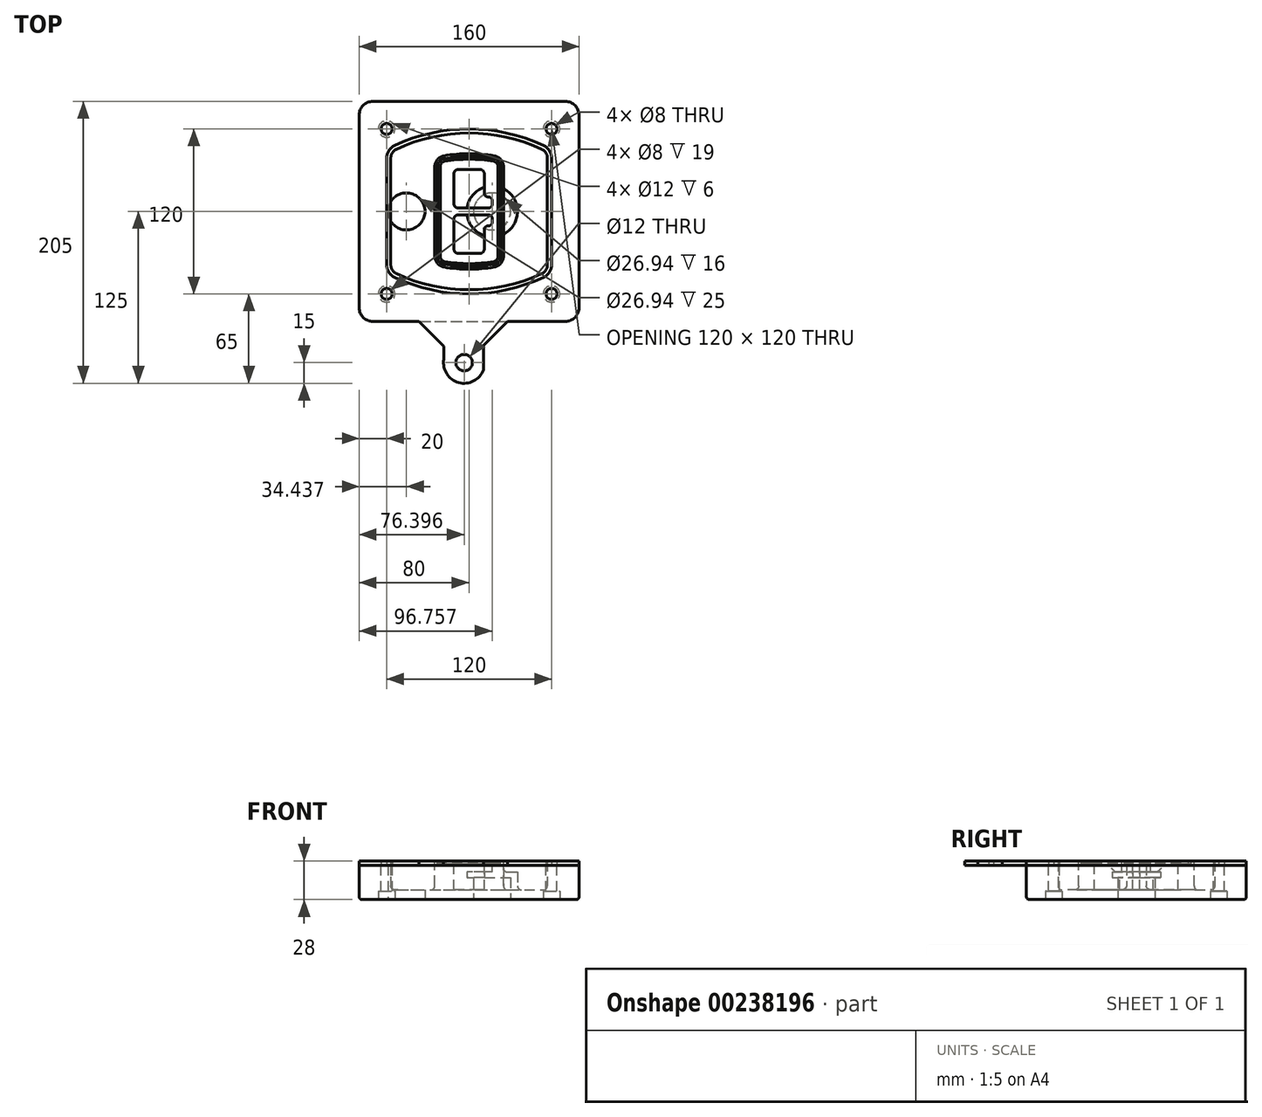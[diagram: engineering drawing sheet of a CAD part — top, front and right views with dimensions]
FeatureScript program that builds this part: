
annotation { "Feature Type Name" : "Feature", "Feature Type Description" : "" }
export const myFeature = defineFeature(function(context is Context, id is Id, definition is map)
    precondition{}
    {
        {
            var Q0;
            Q0=qCreatedBy(makeId("Top.planeOp"),FACE);
            var sketch = newSketch(context, id + "F0", { "sketchPlane" : qUnion([Q0])});
            skPoint(sketch, "E0.rect.middle", {"position": v(0, 0) * mm});
            skLineSegment(sketch, "E1.bottom", {"start": v(-70, -80) * mm, "end": v(70, -80) * mm});
            skLineSegment(sketch, "E1.top", {"start": v(-70, 80) * mm, "end": v(70, 80) * mm});
            skLineSegment(sketch, "E1.left", {"start": v(-80, -70) * mm, "end": v(-80, 70) * mm});
            skLineSegment(sketch, "E1.right", {"start": v(80, -70) * mm, "end": v(80, 70) * mm});
            skLineSegment(sketch, "E2", {"start": v(-80, 80) * mm, "end": v(80, -80) * mm, "construction": true});
            skLineSegment(sketch, "E3", {"start": v(80, 80) * mm, "end": v(-80, -80) * mm, "construction": true});
            skCircle(sketch, "E4", {"center": v(-60, 60) * mm, "radius": 4 * mm});
            skCircle(sketch, "E5", {"center": v(60, 60) * mm, "radius": 4 * mm});
            skCircle(sketch, "E6", {"center": v(60, -60) * mm, "radius": 4 * mm});
            skCircle(sketch, "E7", {"center": v(-60, -60) * mm, "radius": 4 * mm});
            skLineSegment(sketch, "E8", {"start": v(-60, 60) * mm, "end": v(60, 60) * mm, "construction": true});
            skLineSegment(sketch, "E9", {"start": v(60, 60) * mm, "end": v(60, -60) * mm, "construction": true});
            skLineSegment(sketch, "E10", {"start": v(60, -60) * mm, "end": v(-60, -60) * mm, "construction": true});
            skLineSegment(sketch, "E11", {"start": v(-60, -60) * mm, "end": v(-60, 60) * mm, "construction": true});
            skLineSegment(sketch, "E12", {"start": v(-60, 38.83) * mm, "end": v(-60, -38.83) * mm});
            skLineSegment(sketch, "E13", {"start": v(60, 38.83) * mm, "end": v(60, -38.83) * mm});
            skArc(sketch, "E14", {"start": v(54.26, 47.88) * mm, "mid": v(0, 60) * mm, "end": v(-54.26, 47.88) * mm});
            skArc(sketch, "E15", {"start": v(-54.26, -47.88) * mm, "mid": v(0, -60) * mm, "end": v(54.26, -47.88) * mm});
            skLineSegment(sketch, "E16", {"start": v(-60, 0) * mm, "end": v(60, 0) * mm, "construction": true});
            skPoint(sketch, "E17.visualSharp", {"position": v(-60, -45) * mm});
            skArc(sketch, "E17.filletArc", {"start": v(-60, -38.83) * mm, "mid": v(-58.44, -44.2) * mm, "end": v(-54.26, -47.88) * mm});
            skPoint(sketch, "E18.visualSharp", {"position": v(-60, 45) * mm});
            skArc(sketch, "E18.filletArc", {"start": v(-54.26, 47.88) * mm, "mid": v(-58.44, 44.2) * mm, "end": v(-60, 38.83) * mm});
            skPoint(sketch, "E19.visualSharp", {"position": v(60, 45) * mm});
            skArc(sketch, "E19.filletArc", {"start": v(60, 38.83) * mm, "mid": v(58.44, 44.2) * mm, "end": v(54.26, 47.88) * mm});
            skPoint(sketch, "E20.visualSharp", {"position": v(60, -45) * mm});
            skArc(sketch, "E20.filletArc", {"start": v(54.26, -47.88) * mm, "mid": v(58.44, -44.2) * mm, "end": v(60, -38.83) * mm});
            skPoint(sketch, "E21.visualSharp", {"position": v(-80, 80) * mm});
            skArc(sketch, "E21.filletArc", {"start": v(-70, 80) * mm, "mid": v(-77.07, 77.07) * mm, "end": v(-80, 70) * mm});
            skPoint(sketch, "E22.visualSharp", {"position": v(80, 80) * mm});
            skArc(sketch, "E22.filletArc", {"start": v(80, 70) * mm, "mid": v(77.07, 77.07) * mm, "end": v(70, 80) * mm});
            skPoint(sketch, "E23.visualSharp", {"position": v(80, -80) * mm});
            skArc(sketch, "E23.filletArc", {"start": v(70, -80) * mm, "mid": v(77.07, -77.07) * mm, "end": v(80, -70) * mm});
            skPoint(sketch, "E24.visualSharp", {"position": v(-80, -80) * mm});
            skArc(sketch, "E24.filletArc", {"start": v(-80, -70) * mm, "mid": v(-77.07, -77.07) * mm, "end": v(-70, -80) * mm});
            skArc(sketch, "E25.0", {"start": v(57, 38.83) * mm, "mid": v(55.9, 42.58) * mm, "end": v(52.98, 45.17) * mm});
            skLineSegment(sketch, "E25.1", {"start": v(57, 38.83) * mm, "end": v(57, -38.83) * mm});
            skArc(sketch, "E25.2", {"start": v(52.98, -45.17) * mm, "mid": v(55.9, -42.58) * mm, "end": v(57, -38.83) * mm});
            skArc(sketch, "E25.3", {"start": v(-52.98, -45.17) * mm, "mid": v(0, -57) * mm, "end": v(52.98, -45.17) * mm});
            skArc(sketch, "E25.4", {"start": v(-57, -38.83) * mm, "mid": v(-55.9, -42.58) * mm, "end": v(-52.98, -45.17) * mm});
            skArc(sketch, "E25.5", {"start": v(52.98, 45.17) * mm, "mid": v(0, 57) * mm, "end": v(-52.98, 45.17) * mm});
            skLineSegment(sketch, "E25.6", {"start": v(-57, 38.83) * mm, "end": v(-57, -38.83) * mm});
            skArc(sketch, "E25.7", {"start": v(-52.98, 45.17) * mm, "mid": v(-55.9, 42.58) * mm, "end": v(-57, 38.83) * mm});
            skArc(sketch, "E26.0", {"start": v(-55.96, 51.5) * mm, "mid": v(-61.82, 46.33) * mm, "end": v(-64, 38.83) * mm});
            skArc(sketch, "E26.1", {"start": v(55.96, 51.5) * mm, "mid": v(0, 64) * mm, "end": v(-55.96, 51.5) * mm});
            skArc(sketch, "E26.2", {"start": v(64, 38.83) * mm, "mid": v(61.82, 46.33) * mm, "end": v(55.96, 51.5) * mm});
            skLineSegment(sketch, "E26.3", {"start": v(64, 38.83) * mm, "end": v(64, -38.83) * mm});
            skArc(sketch, "E26.4", {"start": v(55.96, -51.5) * mm, "mid": v(61.82, -46.33) * mm, "end": v(64, -38.83) * mm});
            skLineSegment(sketch, "E26.5", {"start": v(-64, 38.83) * mm, "end": v(-64, -38.83) * mm});
            skArc(sketch, "E26.6", {"start": v(-55.96, -51.5) * mm, "mid": v(0, -64) * mm, "end": v(55.96, -51.5) * mm});
            skArc(sketch, "E26.7", {"start": v(-64, -38.83) * mm, "mid": v(-61.82, -46.33) * mm, "end": v(-55.96, -51.5) * mm});
            skSolve(sketch);
        }
        {
            var Q0;
            Q0=makeQuery(id+"F0.imprint","IMPRINT",FACE,{"disambiguationData":[TD([[makeQuery(id+"F0.imprint","IMPRINT",EDGE,{"derivedFrom":sQuery(id+"F0.wireOp",EDGE,"E1.bottom")}),1.0]])]});
            var Q1;
            Q1=makeQuery(id+"F0.imprint","IMPRINT",FACE,{"disambiguationData":[TD([[makeQuery(id+"F0.imprint","IMPRINT",EDGE,{"derivedFrom":sQuery(id+"F0.wireOp",EDGE,"E12")}),1.0]])]});
            var Q2;
            Q2=makeQuery(id+"F0.imprint","IMPRINT",FACE,{"disambiguationData":[TD([[makeQuery(id+"F0.imprint","IMPRINT",EDGE,{"derivedFrom":sQuery(id+"F0.wireOp",EDGE,"E25.0")}),1.0]])]});
            var Q3;
            Q3=makeQuery(id+"F0.imprint","IMPRINT",FACE,{"disambiguationData":[TD([[makeQuery(id+"F0.imprint","IMPRINT",EDGE,{"derivedFrom":sQuery(id+"F0.wireOp",EDGE,"E12")}),-1.0]])]});
            extrude(context, id + "F1", {"entities" : qUnion([Q0, Q1, Q2, Q3]), "oppositeDirection" : true, "depth" : 25 * mm});
        }
        {
            var Q0;
            Q0=makeQuery(id+"F0.imprint","IMPRINT",FACE,{"disambiguationData":[TD([[makeQuery(id+"F0.imprint","IMPRINT",EDGE,{"derivedFrom":sQuery(id+"F0.wireOp",EDGE,"E12")}),1.0]])]});
            extrude(context, id + "F2", {"entities" : qUnion([Q0]), "operationType" : NewBodyOperationType.ADD, "depth" : 3 * mm});
        }
        {
            var Q0;
            Q0=makeQuery(id+"F0.imprint","IMPRINT",FACE,{"disambiguationData":[TD([[makeQuery(id+"F0.imprint","IMPRINT",EDGE,{"derivedFrom":sQuery(id+"F0.wireOp",EDGE,"E25.0")}),1.0]])]});
            extrude(context, id + "F3", {"entities" : qUnion([Q0]), "operationType" : NewBodyOperationType.REMOVE, "oppositeDirection" : true, "depth" : 18 * mm});
        }
        {
            var Q0;
            Q0=makeQuery(id+"F2.opExtrude","CAP_FACE",FACE,{"disambiguationData":[OSD([sQuery(id+"F0.wireOp",EDGE,"E12"),sQuery(id+"F0.wireOp",EDGE,"E13"),sQuery(id+"F0.wireOp",EDGE,"E14"),sQuery(id+"F0.wireOp",EDGE,"E15"),sQuery(id+"F0.wireOp",EDGE,"E17.filletArc"),sQuery(id+"F0.wireOp",EDGE,"E18.filletArc"),sQuery(id+"F0.wireOp",EDGE,"E19.filletArc"),sQuery(id+"F0.wireOp",EDGE,"E20.filletArc"),sQuery(id+"F0.wireOp",EDGE,"E25.0"),sQuery(id+"F0.wireOp",EDGE,"E25.1"),sQuery(id+"F0.wireOp",EDGE,"E25.2"),sQuery(id+"F0.wireOp",EDGE,"E25.3"),sQuery(id+"F0.wireOp",EDGE,"E25.4"),sQuery(id+"F0.wireOp",EDGE,"E25.5"),sQuery(id+"F0.wireOp",EDGE,"E25.6"),sQuery(id+"F0.wireOp",EDGE,"E25.7")])],"isStart":false});
            var sketch = newSketch(context, id + "F4", { "sketchPlane" : qUnion([Q0])});
            skArc(sketch, "E27.0", {"start": v(-18.34, -40.45) * mm, "mid": v(0, -42) * mm, "end": v(18.34, -40.45) * mm});
            skArc(sketch, "E28.0", {"start": v(18.34, 40.45) * mm, "mid": v(0, 42) * mm, "end": v(-18.34, 40.45) * mm});
            skLineSegment(sketch, "E29", {"start": v(-25, 32.57) * mm, "end": v(-25, -32.57) * mm});
            skLineSegment(sketch, "E30", {"start": v(25, 32.57) * mm, "end": v(25, -32.57) * mm});
            skLineSegment(sketch, "E31", {"start": v(-25, 39.1) * mm, "end": v(25, 39.1) * mm, "construction": true});
            skLineSegment(sketch, "E32", {"start": v(-25, -39.1) * mm, "end": v(25, -39.1) * mm, "construction": true});
            skPoint(sketch, "E33.visualSharp", {"position": v(-25, 39.1) * mm});
            skArc(sketch, "E33.filletArc", {"start": v(-18.34, 40.45) * mm, "mid": v(-23.11, 37.73) * mm, "end": v(-25, 32.57) * mm});
            skPoint(sketch, "E34.visualSharp", {"position": v(25, 39.1) * mm});
            skArc(sketch, "E34.filletArc", {"start": v(25, 32.57) * mm, "mid": v(23.11, 37.73) * mm, "end": v(18.34, 40.45) * mm});
            skPoint(sketch, "E35.visualSharp", {"position": v(25, -39.1) * mm});
            skArc(sketch, "E35.filletArc", {"start": v(18.34, -40.45) * mm, "mid": v(23.11, -37.73) * mm, "end": v(25, -32.57) * mm});
            skPoint(sketch, "E36.visualSharp", {"position": v(-25, -39.1) * mm});
            skArc(sketch, "E36.filletArc", {"start": v(-25, -32.57) * mm, "mid": v(-23.11, -37.73) * mm, "end": v(-18.34, -40.45) * mm});
            skArc(sketch, "E37.0", {"start": v(52.98, 45.17) * mm, "mid": v(0, 57) * mm, "end": v(-52.98, 45.17) * mm});
            skArc(sketch, "E37.1", {"start": v(-52.98, 45.17) * mm, "mid": v(-55.9, 42.58) * mm, "end": v(-57, 38.83) * mm});
            skLineSegment(sketch, "E37.2", {"start": v(-57, 38.83) * mm, "end": v(-57, -38.83) * mm});
            skArc(sketch, "E37.3", {"start": v(-57, -38.83) * mm, "mid": v(-55.9, -42.58) * mm, "end": v(-52.98, -45.17) * mm});
            skArc(sketch, "E37.4", {"start": v(-52.98, -45.17) * mm, "mid": v(0, -57) * mm, "end": v(52.98, -45.17) * mm});
            skArc(sketch, "E37.5", {"start": v(52.98, -45.17) * mm, "mid": v(55.9, -42.58) * mm, "end": v(57, -38.83) * mm});
            skLineSegment(sketch, "E37.6", {"start": v(57, 38.83) * mm, "end": v(57, -38.83) * mm});
            skArc(sketch, "E37.7", {"start": v(57, 38.83) * mm, "mid": v(55.9, 42.58) * mm, "end": v(52.98, 45.17) * mm});
            skLineSegment(sketch, "E38.0", {"start": v(23, 32.57) * mm, "end": v(23, -32.57) * mm});
            skArc(sketch, "E38.1", {"start": v(18, -38.48) * mm, "mid": v(21.58, -36.44) * mm, "end": v(23, -32.57) * mm});
            skArc(sketch, "E38.2", {"start": v(-18, -38.48) * mm, "mid": v(0, -40) * mm, "end": v(18, -38.48) * mm});
            skArc(sketch, "E38.3", {"start": v(-23, -32.57) * mm, "mid": v(-21.58, -36.44) * mm, "end": v(-18, -38.48) * mm});
            skLineSegment(sketch, "E38.4", {"start": v(-23, 32.57) * mm, "end": v(-23, -32.57) * mm});
            skArc(sketch, "E38.5", {"start": v(23, 32.57) * mm, "mid": v(21.58, 36.44) * mm, "end": v(18, 38.48) * mm});
            skArc(sketch, "E38.6", {"start": v(-18, 38.48) * mm, "mid": v(-21.58, 36.44) * mm, "end": v(-23, 32.57) * mm});
            skArc(sketch, "E38.7", {"start": v(18, 38.48) * mm, "mid": v(0, 40) * mm, "end": v(-18, 38.48) * mm});
            skArc(sketch, "E39.0", {"start": v(21, 32.57) * mm, "mid": v(20.06, 35.15) * mm, "end": v(17.67, 36.5) * mm});
            skLineSegment(sketch, "E39.1", {"start": v(21, 32.57) * mm, "end": v(21, -32.57) * mm});
            skArc(sketch, "E39.2", {"start": v(17.67, -36.5) * mm, "mid": v(20.06, -35.15) * mm, "end": v(21, -32.57) * mm});
            skArc(sketch, "E39.3", {"start": v(-17.67, -36.5) * mm, "mid": v(0, -38) * mm, "end": v(17.67, -36.5) * mm});
            skArc(sketch, "E39.4", {"start": v(-21, -32.57) * mm, "mid": v(-20.06, -35.15) * mm, "end": v(-17.67, -36.5) * mm});
            skArc(sketch, "E39.5", {"start": v(17.67, 36.5) * mm, "mid": v(0, 38) * mm, "end": v(-17.67, 36.5) * mm});
            skLineSegment(sketch, "E39.6", {"start": v(-21, 32.57) * mm, "end": v(-21, -32.57) * mm});
            skArc(sketch, "E39.7", {"start": v(-17.67, 36.5) * mm, "mid": v(-20.06, 35.15) * mm, "end": v(-21, 32.57) * mm});
            skLineSegment(sketch, "E40", {"start": v(-25, 0) * mm, "end": v(25, 0) * mm, "construction": true});
            skLineSegment(sketch, "E41", {"start": v(-11, 5.5) * mm, "end": v(-11, 27.5) * mm});
            skLineSegment(sketch, "E42", {"start": v(-8, 30.5) * mm, "end": v(8, 30.5) * mm});
            skLineSegment(sketch, "E43", {"start": v(11, 27.5) * mm, "end": v(11, 13.5) * mm});
            skLineSegment(sketch, "E44", {"start": v(14, 10.5) * mm, "end": v(14, 10.5) * mm});
            skLineSegment(sketch, "E45", {"start": v(17, 7.5) * mm, "end": v(17, 5.5) * mm});
            skLineSegment(sketch, "E46", {"start": v(14, 2.5) * mm, "end": v(-8, 2.5) * mm});
            skPoint(sketch, "E47.visualSharp", {"position": v(-11, 30.5) * mm});
            skArc(sketch, "E47.filletArc", {"start": v(-8, 30.5) * mm, "mid": v(-10.12, 29.62) * mm, "end": v(-11, 27.5) * mm});
            skPoint(sketch, "E48.visualSharp", {"position": v(11, 30.5) * mm});
            skArc(sketch, "E48.filletArc", {"start": v(11, 27.5) * mm, "mid": v(10.12, 29.62) * mm, "end": v(8, 30.5) * mm});
            skPoint(sketch, "E49.visualSharp", {"position": v(11, 10.5) * mm});
            skArc(sketch, "E49.filletArc", {"start": v(11, 13.5) * mm, "mid": v(11.88, 11.38) * mm, "end": v(14, 10.5) * mm});
            skPoint(sketch, "E50.visualSharp", {"position": v(17, 10.5) * mm});
            skArc(sketch, "E50.filletArc", {"start": v(17, 7.5) * mm, "mid": v(16.12, 9.62) * mm, "end": v(14, 10.5) * mm});
            skPoint(sketch, "E51.visualSharp", {"position": v(17, 2.5) * mm});
            skArc(sketch, "E51.filletArc", {"start": v(14, 2.5) * mm, "mid": v(16.12, 3.38) * mm, "end": v(17, 5.5) * mm});
            skPoint(sketch, "E52.visualSharp", {"position": v(-11, 2.5) * mm});
            skArc(sketch, "E52.filletArc", {"start": v(-11, 5.5) * mm, "mid": v(-10.12, 3.38) * mm, "end": v(-8, 2.5) * mm});
            skLineSegment(sketch, "E53.0.MirrorCS", {"start": v(14, -2.5) * mm, "end": v(-8, -2.5) * mm});
            skArc(sketch, "E54.0.MirrorCS", {"start": v(-11, -5.5) * mm, "mid": v(-10.12, -3.38) * mm, "end": v(-8, -2.5) * mm});
            skLineSegment(sketch, "E55.0.MirrorCS", {"start": v(-11, -5.5) * mm, "end": v(-11, -27.5) * mm});
            skArc(sketch, "E56.0.MirrorCS", {"start": v(-8, -30.5) * mm, "mid": v(-10.12, -29.62) * mm, "end": v(-11, -27.5) * mm});
            skLineSegment(sketch, "E57.0.MirrorCS", {"start": v(-8, -30.5) * mm, "end": v(8, -30.5) * mm});
            skArc(sketch, "E58.0.MirrorCS", {"start": v(11, -27.5) * mm, "mid": v(10.12, -29.62) * mm, "end": v(8, -30.5) * mm});
            skLineSegment(sketch, "E59.0.MirrorCS", {"start": v(11, -27.5) * mm, "end": v(11, -13.5) * mm});
            skArc(sketch, "E60.0.MirrorCS", {"start": v(11, -13.5) * mm, "mid": v(11.88, -11.38) * mm, "end": v(14, -10.5) * mm});
            skArc(sketch, "E61.0.MirrorCS", {"start": v(17, -7.5) * mm, "mid": v(16.12, -9.62) * mm, "end": v(14, -10.5) * mm});
            skLineSegment(sketch, "E62.0.MirrorCS", {"start": v(17, -7.5) * mm, "end": v(17, -5.5) * mm});
            skArc(sketch, "E63.0.MirrorCS", {"start": v(14, -2.5) * mm, "mid": v(16.12, -3.38) * mm, "end": v(17, -5.5) * mm});
            skSolve(sketch);
        }
        {
            var Q0;
            Q0=makeQuery(id+"F4.imprint","IMPRINT",FACE,{"disambiguationData":[TD([[makeQuery(id+"F4.imprint","IMPRINT",EDGE,{"derivedFrom":sQuery(id+"F4.wireOp",EDGE,"E27.0")}),1.0]])]});
            var Q1;
            Q1=makeQuery(id+"F4.imprint","IMPRINT",FACE,{"disambiguationData":[TD([[makeQuery(id+"F4.imprint","IMPRINT",EDGE,{"derivedFrom":sQuery(id+"F4.wireOp",EDGE,"E38.0")}),-1.0]])]});
            var Q2;
            Q2=makeQuery(id+"F4.imprint","IMPRINT",FACE,{"disambiguationData":[TD([[makeQuery(id+"F4.imprint","IMPRINT",EDGE,{"derivedFrom":sQuery(id+"F4.wireOp",EDGE,"E39.0")}),1.0]])]});
            extrude(context, id + "F5", {"entities" : qUnion([Q0, Q1, Q2]), "operationType" : NewBodyOperationType.ADD, "endBound" : BoundingType.UP_TO_NEXT, "oppositeDirection" : true, "depth" : 25 * mm});
        }
        {
            var Q0;
            Q0=makeQuery(id+"F4.imprint","IMPRINT",FACE,{"disambiguationData":[TD([[makeQuery(id+"F4.imprint","IMPRINT",EDGE,{"derivedFrom":sQuery(id+"F4.wireOp",EDGE,"E38.0")}),-1.0]])]});
            extrude(context, id + "F6", {"entities" : qUnion([Q0]), "operationType" : NewBodyOperationType.REMOVE, "oppositeDirection" : true, "depth" : 2 * mm});
        }
        {
            var Q0;
            Q0=makeQuery(id+"F1.opExtrude","CAP_FACE",FACE,{"disambiguationData":[OSD([sQuery(id+"F0.wireOp",EDGE,"E1.bottom"),sQuery(id+"F0.wireOp",EDGE,"E1.top"),sQuery(id+"F0.wireOp",EDGE,"E1.left"),sQuery(id+"F0.wireOp",EDGE,"E1.right"),sQuery(id+"F0.wireOp",EDGE,"E4"),sQuery(id+"F0.wireOp",EDGE,"E5"),sQuery(id+"F0.wireOp",EDGE,"E6"),sQuery(id+"F0.wireOp",EDGE,"E7"),sQuery(id+"F0.wireOp",EDGE,"E21.filletArc"),sQuery(id+"F0.wireOp",EDGE,"E22.filletArc"),sQuery(id+"F0.wireOp",EDGE,"E23.filletArc"),sQuery(id+"F0.wireOp",EDGE,"E24.filletArc")])],"isStart":false});
            var sketch = newSketch(context, id + "F7", { "sketchPlane" : qUnion([Q0])});
            skCircle(sketch, "E64", {"center": v(16.76, 0) * mm, "radius": 13.47 * mm});
            skCircle(sketch, "E65", {"center": v(-45.56, 0) * mm, "radius": 13.47 * mm});
            skLineSegment(sketch, "E66", {"start": v(80, 0) * mm, "end": v(-80, 0) * mm});
            skCircle(sketch, "E67", {"center": v(16.76, 0) * mm, "radius": 18.47 * mm});
            skCircle(sketch, "E68", {"center": v(60, -60) * mm, "radius": 6 * mm});
            skCircle(sketch, "E69", {"center": v(-60, -60) * mm, "radius": 6 * mm});
            skCircle(sketch, "E70", {"center": v(-60, 60) * mm, "radius": 6 * mm});
            skCircle(sketch, "E71", {"center": v(60, 60) * mm, "radius": 6 * mm});
            skSolve(sketch);
        }
        {
            var Q0;
            {var subQ1=sQuery(id+"F7.wireOp",EDGE,"E66");var subQ4=sQuery(id+"F7.wireOp",EDGE,"E64");var subQ6=makeQuery(id+"F7.imprint","INTERSECT",VERTEX,{"disambiguationData":[OD(0.0)],"derivedFrom":[subQ4,subQ1]});Q0=makeQuery(id+"F7.imprint","IMPRINT",FACE,{"disambiguationData":[TD([[makeQuery(id+"F7.imprint","IMPRINT",EDGE,{"disambiguationData":[TD([[subQ6,-1.0]])],"derivedFrom":subQ4}),-1.0]])]});}
            var Q1;
            {var subQ0=sQuery(id+"F7.wireOp",EDGE,"E66");var subQ1=sQuery(id+"F7.wireOp",EDGE,"E64");var subQ3=makeQuery(id+"F7.imprint","INTERSECT",VERTEX,{"disambiguationData":[OD(0.0)],"derivedFrom":[subQ1,subQ0]});Q1=makeQuery(id+"F7.imprint","IMPRINT",FACE,{"disambiguationData":[TD([[makeQuery(id+"F7.imprint","IMPRINT",EDGE,{"disambiguationData":[TD([[subQ3,-1.0]])],"derivedFrom":subQ1}),1.0]])]});}
            var Q2;
            {var subQ0=sQuery(id+"F7.wireOp",EDGE,"E66");var subQ1=sQuery(id+"F7.wireOp",EDGE,"E64");var subQ3=makeQuery(id+"F7.imprint","INTERSECT",VERTEX,{"disambiguationData":[OD(0.0)],"derivedFrom":[subQ1,subQ0]});Q2=makeQuery(id+"F7.imprint","IMPRINT",FACE,{"disambiguationData":[TD([[makeQuery(id+"F7.imprint","IMPRINT",EDGE,{"disambiguationData":[TD([[subQ3,1.0]])],"derivedFrom":subQ1}),1.0]])]});}
            var Q3;
            {var subQ1=sQuery(id+"F7.wireOp",EDGE,"E66");var subQ4=sQuery(id+"F7.wireOp",EDGE,"E64");var subQ6=makeQuery(id+"F7.imprint","INTERSECT",VERTEX,{"disambiguationData":[OD(0.0)],"derivedFrom":[subQ4,subQ1]});Q3=makeQuery(id+"F7.imprint","IMPRINT",FACE,{"disambiguationData":[TD([[makeQuery(id+"F7.imprint","IMPRINT",EDGE,{"disambiguationData":[TD([[subQ6,1.0]])],"derivedFrom":subQ4}),-1.0]])]});}
            extrude(context, id + "F8", {"entities" : qUnion([Q0, Q1, Q2, Q3]), "operationType" : NewBodyOperationType.ADD, "oppositeDirection" : true, "depth" : 20 * mm});
        }
        {
            var Q0;
            {var subQ0=sQuery(id+"F7.wireOp",EDGE,"E66");var subQ1=sQuery(id+"F7.wireOp",EDGE,"E64");var subQ3=makeQuery(id+"F7.imprint","INTERSECT",VERTEX,{"disambiguationData":[OD(0.0)],"derivedFrom":[subQ1,subQ0]});Q0=makeQuery(id+"F7.imprint","IMPRINT",FACE,{"disambiguationData":[TD([[makeQuery(id+"F7.imprint","IMPRINT",EDGE,{"disambiguationData":[TD([[subQ3,-1.0]])],"derivedFrom":subQ1}),1.0]])]});}
            var Q1;
            {var subQ0=sQuery(id+"F7.wireOp",EDGE,"E66");var subQ1=sQuery(id+"F7.wireOp",EDGE,"E64");var subQ3=makeQuery(id+"F7.imprint","INTERSECT",VERTEX,{"disambiguationData":[OD(0.0)],"derivedFrom":[subQ1,subQ0]});Q1=makeQuery(id+"F7.imprint","IMPRINT",FACE,{"disambiguationData":[TD([[makeQuery(id+"F7.imprint","IMPRINT",EDGE,{"disambiguationData":[TD([[subQ3,1.0]])],"derivedFrom":subQ1}),1.0]])]});}
            extrude(context, id + "F9", {"entities" : qUnion([Q0, Q1]), "operationType" : NewBodyOperationType.REMOVE, "oppositeDirection" : true, "depth" : 16 * mm});
        }
        {
            var Q0;
            {var subQ0=sQuery(id+"F7.wireOp",EDGE,"E66");var subQ1=sQuery(id+"F7.wireOp",EDGE,"E65");var subQ3=makeQuery(id+"F7.imprint","INTERSECT",VERTEX,{"disambiguationData":[OD(0.0)],"derivedFrom":[subQ1,subQ0]});Q0=makeQuery(id+"F7.imprint","IMPRINT",FACE,{"disambiguationData":[TD([[makeQuery(id+"F7.imprint","IMPRINT",EDGE,{"disambiguationData":[TD([[subQ3,-1.0]])],"derivedFrom":subQ1}),1.0]])]});}
            var Q1;
            {var subQ0=sQuery(id+"F7.wireOp",EDGE,"E66");var subQ1=sQuery(id+"F7.wireOp",EDGE,"E65");var subQ3=makeQuery(id+"F7.imprint","INTERSECT",VERTEX,{"disambiguationData":[OD(0.0)],"derivedFrom":[subQ1,subQ0]});Q1=makeQuery(id+"F7.imprint","IMPRINT",FACE,{"disambiguationData":[TD([[makeQuery(id+"F7.imprint","IMPRINT",EDGE,{"disambiguationData":[TD([[subQ3,1.0]])],"derivedFrom":subQ1}),1.0]])]});}
            extrude(context, id + "F10", {"entities" : qUnion([Q0, Q1]), "operationType" : NewBodyOperationType.REMOVE, "oppositeDirection" : true, "depth" : 25 * mm});
        }
        {
            var Q0;
            Q0=makeQuery(id+"F7.imprint","IMPRINT",FACE,{"disambiguationData":[TD([[makeQuery(id+"F7.imprint","IMPRINT",EDGE,{"derivedFrom":sQuery(id+"F7.wireOp",EDGE,"E68")}),1.0]])]});
            var Q1;
            Q1=makeQuery(id+"F7.imprint","IMPRINT",FACE,{"disambiguationData":[TD([[makeQuery(id+"F7.imprint","IMPRINT",EDGE,{"derivedFrom":makeQuery(id+"F1.opExtrude","CAP_EDGE",EDGE,{"disambiguationData":[OSD([sQuery(id+"F0.wireOp",EDGE,"E5")])],"isStart":false})}),-1.0]])]});
            var Q2;
            Q2=makeQuery(id+"F7.imprint","IMPRINT",FACE,{"disambiguationData":[TD([[makeQuery(id+"F7.imprint","IMPRINT",EDGE,{"derivedFrom":sQuery(id+"F7.wireOp",EDGE,"E69")}),1.0]])]});
            var Q3;
            Q3=makeQuery(id+"F7.imprint","IMPRINT",FACE,{"disambiguationData":[TD([[makeQuery(id+"F7.imprint","IMPRINT",EDGE,{"derivedFrom":makeQuery(id+"F1.opExtrude","CAP_EDGE",EDGE,{"disambiguationData":[OSD([sQuery(id+"F0.wireOp",EDGE,"E4")])],"isStart":false})}),-1.0]])]});
            var Q4;
            Q4=makeQuery(id+"F7.imprint","IMPRINT",FACE,{"disambiguationData":[TD([[makeQuery(id+"F7.imprint","IMPRINT",EDGE,{"derivedFrom":sQuery(id+"F7.wireOp",EDGE,"E70")}),1.0]])]});
            var Q5;
            Q5=makeQuery(id+"F7.imprint","IMPRINT",FACE,{"disambiguationData":[TD([[makeQuery(id+"F7.imprint","IMPRINT",EDGE,{"derivedFrom":makeQuery(id+"F1.opExtrude","CAP_EDGE",EDGE,{"disambiguationData":[OSD([sQuery(id+"F0.wireOp",EDGE,"E7")])],"isStart":false})}),-1.0]])]});
            var Q6;
            Q6=makeQuery(id+"F7.imprint","IMPRINT",FACE,{"disambiguationData":[TD([[makeQuery(id+"F7.imprint","IMPRINT",EDGE,{"derivedFrom":sQuery(id+"F7.wireOp",EDGE,"E71")}),1.0]])]});
            var Q7;
            Q7=makeQuery(id+"F7.imprint","IMPRINT",FACE,{"disambiguationData":[TD([[makeQuery(id+"F7.imprint","IMPRINT",EDGE,{"derivedFrom":makeQuery(id+"F1.opExtrude","CAP_EDGE",EDGE,{"disambiguationData":[OSD([sQuery(id+"F0.wireOp",EDGE,"E6")])],"isStart":false})}),-1.0]])]});
            extrude(context, id + "F11", {"entities" : qUnion([Q0, Q1, Q2, Q3, Q4, Q5, Q6, Q7]), "operationType" : NewBodyOperationType.REMOVE, "oppositeDirection" : true, "depth" : 6 * mm});
        }
        {
            var Q0;
            Q0=makeQuery(id+"F9.boolean.opBoolean","COPY",FACE,{"derivedFrom":makeQuery(id+"F9.opExtrude","CAP_FACE",FACE,{"disambiguationData":[OSD([sQuery(id+"F7.wireOp",EDGE,"E64")])],"isStart":false})});
            var sketch = newSketch(context, id + "F12", { "sketchPlane" : qUnion([Q0])});
            skArc(sketch, "E72.0", {"start": v(11, 17.55) * mm, "mid": v(2.57, 11.82) * mm, "end": v(-1.54, 2.5) * mm});
            skArc(sketch, "E72.1", {"start": v(-1.54, -2.5) * mm, "mid": v(2.57, -11.82) * mm, "end": v(11, -17.55) * mm});
            skLineSegment(sketch, "E73", {"start": v(-1.54, -2.5) * mm, "end": v(14, -2.5) * mm});
            skLineSegment(sketch, "E74.0", {"start": v(14, 2.5) * mm, "end": v(-1.54, 2.5) * mm});
            skArc(sketch, "E74.1", {"start": v(14, 2.5) * mm, "mid": v(16.12, 3.38) * mm, "end": v(17, 5.5) * mm});
            skLineSegment(sketch, "E74.2", {"start": v(17, 7.5) * mm, "end": v(17, 5.5) * mm});
            skArc(sketch, "E74.3", {"start": v(17, 7.5) * mm, "mid": v(16.12, 9.62) * mm, "end": v(14, 10.5) * mm});
            skArc(sketch, "E74.4", {"start": v(11, 13.5) * mm, "mid": v(11.88, 11.38) * mm, "end": v(14, 10.5) * mm});
            skLineSegment(sketch, "E74.5", {"start": v(11, 17.55) * mm, "end": v(11, 13.5) * mm});
            skLineSegment(sketch, "E74.7", {"start": v(14, -2.5) * mm, "end": v(-1.54, -2.5) * mm});
            skArc(sketch, "E74.8", {"start": v(14, -2.5) * mm, "mid": v(16.12, -3.38) * mm, "end": v(17, -5.5) * mm});
            skLineSegment(sketch, "E74.9", {"start": v(17, -7.5) * mm, "end": v(17, -5.5) * mm});
            skArc(sketch, "E74.10", {"start": v(17, -7.5) * mm, "mid": v(16.12, -9.62) * mm, "end": v(14, -10.5) * mm});
            skArc(sketch, "E74.11", {"start": v(11, -13.5) * mm, "mid": v(11.88, -11.38) * mm, "end": v(14, -10.5) * mm});
            skLineSegment(sketch, "E74.12", {"start": v(11, -17.55) * mm, "end": v(11, -13.5) * mm});
            skPoint(sketch, "E75.orphan", {"position": v(11, -27.5) * mm});
            skPoint(sketch, "E76.orphan", {"position": v(-8, -2.5) * mm});
            skPoint(sketch, "E77.orphan", {"position": v(-8, 2.5) * mm});
            skPoint(sketch, "E78.orphan", {"position": v(11, 27.5) * mm});
            skSolve(sketch);
        }
        {
            var Q0;
            {var subQ7=sQuery(id+"F12.wireOp",EDGE,"E72.0");var subQ14=sQuery(id+"F12.wireOp",EDGE,"E72.1");var subQ16=sQuery(id+"F12.wireOp",EDGE,"E74.1");var subQ18=sQuery(id+"F12.wireOp",EDGE,"E74.8");Q0=qUnion([makeQuery(id+"F12.imprint","IMPRINT",FACE,{"disambiguationData":[TD([[makeQuery(id+"F12.imprint","IMPRINT",EDGE,{"derivedFrom":subQ7}),1.0]])]}),makeQuery(id+"F12.imprint","IMPRINT",FACE,{"disambiguationData":[TD([[makeQuery(id+"F12.imprint","IMPRINT",EDGE,{"derivedFrom":subQ14}),1.0]])]}),makeQuery(id+"F12.imprint","IMPRINT",FACE,{"disambiguationData":[TD([[makeQuery(id+"F12.imprint","IMPRINT",EDGE,{"derivedFrom":subQ16}),1.0]])]}),makeQuery(id+"F12.imprint","IMPRINT",FACE,{"disambiguationData":[TD([[makeQuery(id+"F12.imprint","IMPRINT",EDGE,{"derivedFrom":subQ18}),-1.0]])]})]);}
            var Q1;
            Q1=makeQuery(id+"F5.boolean.opBoolean","SPLIT",FACE,{"disambiguationData":[TD([makeQuery(id+"F5.opExtrude","SWEPT_FACE",FACE,{"disambiguationData":[OSD([sQuery(id+"F4.wireOp",EDGE,"E41")])]})])],"derivedFrom":makeQuery(id+"F3.boolean.opBoolean","COPY",FACE,{"derivedFrom":makeQuery(id+"F3.opExtrude","CAP_FACE",FACE,{"disambiguationData":[OSD([sQuery(id+"F0.wireOp",EDGE,"E25.0"),sQuery(id+"F0.wireOp",EDGE,"E25.1"),sQuery(id+"F0.wireOp",EDGE,"E25.2"),sQuery(id+"F0.wireOp",EDGE,"E25.3"),sQuery(id+"F0.wireOp",EDGE,"E25.4"),sQuery(id+"F0.wireOp",EDGE,"E25.5"),sQuery(id+"F0.wireOp",EDGE,"E25.6"),sQuery(id+"F0.wireOp",EDGE,"E25.7")])],"isStart":false})})});
            extrude(context, id + "F13", {"entities" : qUnion([Q0]), "operationType" : NewBodyOperationType.REMOVE, "endBound" : BoundingType.UP_TO_SURFACE, "endBoundEntityFace" : qUnion([Q1]), "depth" : 25 * mm});
        }
        {
            var Q0;
            Q0=makeQuery(id+"F3.boolean.opBoolean","COPY",EDGE,{"derivedFrom":makeQuery(id+"F3.opExtrude","CAP_EDGE",EDGE,{"disambiguationData":[OSD([sQuery(id+"F0.wireOp",EDGE,"E25.6")])],"isStart":false})});
            var Q1;
            Q1=makeQuery(id+"F8.boolean.opBoolean","INTERSECT",EDGE,{"derivedFrom":[makeQuery(id+"F5.opExtrude","SWEPT_FACE",FACE,{"disambiguationData":[OSD([sQuery(id+"F4.wireOp",EDGE,"E30")])]}),makeQuery(id+"F8.opExtrude","CAP_FACE",FACE,{"disambiguationData":[OSD([sQuery(id+"F7.wireOp",EDGE,"E67")])],"isStart":false})]});
            var Q2;
            Q2=makeQuery(id+"F8.boolean.opBoolean","INTERSECT",EDGE,{"disambiguationData":[OD(1.0)],"derivedFrom":[makeQuery(id+"F5.opExtrude","SWEPT_FACE",FACE,{"disambiguationData":[OSD([sQuery(id+"F4.wireOp",EDGE,"E30")])]}),makeQuery(id+"F8.opExtrude","SWEPT_FACE",FACE,{"disambiguationData":[OSD([sQuery(id+"F7.wireOp",EDGE,"E67")])]})]});
            var Q3;
            {var subQ0=sQuery(id+"F4.wireOp",EDGE,"E30");Q3=makeQuery(id+"F8.boolean.opBoolean","SPLIT",EDGE,{"disambiguationData":[TD([makeQuery(id+"F5.opExtrude","SWEPT_FACE",FACE,{"disambiguationData":[OSD([sQuery(id+"F4.wireOp",EDGE,"E35.filletArc")])]})])],"derivedFrom":makeQuery(id+"F5.opExtrude","CAP_EDGE",EDGE,{"disambiguationData":[OSD([subQ0])],"isStart":false})});}
            var Q4;
            {var subQ0=sQuery(id+"F0.wireOp",EDGE,"E25.7");var subQ1=sQuery(id+"F0.wireOp",EDGE,"E25.1");var subQ2=sQuery(id+"F0.wireOp",EDGE,"E25.6");var subQ3=sQuery(id+"F0.wireOp",EDGE,"E25.5");var subQ4=sQuery(id+"F0.wireOp",EDGE,"E25.4");var subQ5=sQuery(id+"F0.wireOp",EDGE,"E25.0");var subQ6=sQuery(id+"F0.wireOp",EDGE,"E25.2");var subQ7=sQuery(id+"F0.wireOp",EDGE,"E25.3");Q4=makeQuery(id+"F8.boolean.opBoolean","INTERSECT",EDGE,{"derivedFrom":[makeQuery(id+"F5.boolean.opBoolean","SPLIT",FACE,{"disambiguationData":[TD([makeQuery(id+"F2.opExtrude","SWEPT_FACE",FACE,{"disambiguationData":[OSD([subQ5])]})])],"derivedFrom":makeQuery(id+"F3.boolean.opBoolean","COPY",FACE,{"derivedFrom":makeQuery(id+"F3.opExtrude","CAP_FACE",FACE,{"disambiguationData":[OSD([subQ5,subQ1,subQ6,subQ7,subQ4,subQ3,subQ2,subQ0])],"isStart":false})})}),makeQuery(id+"F8.opExtrude","SWEPT_FACE",FACE,{"disambiguationData":[OSD([sQuery(id+"F7.wireOp",EDGE,"E67")])]})]});}
            var Q5;
            Q5=makeQuery(id+"F8.boolean.opBoolean","INTERSECT",EDGE,{"disambiguationData":[OD(0.0)],"derivedFrom":[makeQuery(id+"F5.opExtrude","SWEPT_FACE",FACE,{"disambiguationData":[OSD([sQuery(id+"F4.wireOp",EDGE,"E30")])]}),makeQuery(id+"F8.opExtrude","SWEPT_FACE",FACE,{"disambiguationData":[OSD([sQuery(id+"F7.wireOp",EDGE,"E67")])]})]});
            fillet(context, id + "F14", {"entities" : qUnion([Q0, Q1, Q2, Q3, Q4, Q5]), "radius" : 3 * mm, "tangentPropagation" : true, "allowEdgeOverflow" : false});
        }
        {
            var Q0;
            Q0=makeQuery(id+"F1.opExtrude","CAP_EDGE",EDGE,{"disambiguationData":[OSD([sQuery(id+"F0.wireOp",EDGE,"E1.bottom")])],"isStart":false});
            fillet(context, id + "F15", {"entities" : qUnion([Q0]), "radius" : 2 * mm, "tangentPropagation" : true, "allowEdgeOverflow" : false});
        }
        {
            var Q0;
            {var subQ0=sQuery(id+"F0.wireOp",EDGE,"E22.filletArc");var subQ1=sQuery(id+"F0.wireOp",EDGE,"E7");var subQ2=sQuery(id+"F0.wireOp",EDGE,"E6");var subQ3=sQuery(id+"F0.wireOp",EDGE,"E5");var subQ4=sQuery(id+"F0.wireOp",EDGE,"E4");var subQ5=sQuery(id+"F0.wireOp",EDGE,"E1.bottom");var subQ6=sQuery(id+"F0.wireOp",EDGE,"E21.filletArc");var subQ7=sQuery(id+"F0.wireOp",EDGE,"E1.top");var subQ8=sQuery(id+"F0.wireOp",EDGE,"E1.left");var subQ9=sQuery(id+"F0.wireOp",EDGE,"E1.right");var subQ10=sQuery(id+"F0.wireOp",EDGE,"E23.filletArc");var subQ11=sQuery(id+"F0.wireOp",EDGE,"E24.filletArc");Q0=makeQuery(id+"F2.boolean.opBoolean","SPLIT",FACE,{"disambiguationData":[TD([makeQuery(id+"F1.opExtrude","SWEPT_FACE",FACE,{"disambiguationData":[OSD([subQ5])]})])],"derivedFrom":makeQuery(id+"F1.opExtrude","CAP_FACE",FACE,{"disambiguationData":[OSD([subQ5,subQ7,subQ8,subQ9,subQ4,subQ3,subQ2,subQ1,subQ6,subQ0,subQ10,subQ11])],"isStart":true})});}
            var sketch = newSketch(context, id + "F16", { "sketchPlane" : qUnion([Q0])});
            skLineSegment(sketch, "E79.0", {"start": v(-70, 80) * mm, "end": v(70, 80) * mm});
            skArc(sketch, "E79.1", {"start": v(-70, 80) * mm, "mid": v(-77.07, 77.07) * mm, "end": v(-80, 70) * mm});
            skLineSegment(sketch, "E79.2", {"start": v(-80, -70) * mm, "end": v(-80, 70) * mm});
            skArc(sketch, "E79.3", {"start": v(80, 70) * mm, "mid": v(77.07, 77.07) * mm, "end": v(70, 80) * mm});
            skLineSegment(sketch, "E79.4", {"start": v(80, -70) * mm, "end": v(80, 70) * mm});
            skCircle(sketch, "E79.5", {"center": v(-60, 60) * mm, "radius": 4 * mm});
            skLineSegment(sketch, "E80", {"start": v(-4.25, 80) * mm, "end": v(0, 80) * mm});
            skLineSegment(sketch, "E81", {"start": v(0, 80) * mm, "end": v(0, 80.9) * mm});
            skLineSegment(sketch, "E82", {"start": v(-36.4, 80) * mm, "end": v(-18.4, 98) * mm});
            skLineSegment(sketch, "E83", {"start": v(28, 80) * mm, "end": v(10.43, 97.57) * mm});
            skLineSegment(sketch, "E84", {"start": v(-18.4, 98) * mm, "end": v(-18.4, 107.55) * mm});
            skLineSegment(sketch, "E85", {"start": v(10.43, 97.57) * mm, "end": v(10.43, 115.3) * mm});
            skArc(sketch, "E86", {"start": v(10.43, 115.3) * mm, "mid": v(-7.5, 124.49) * mm, "end": v(-18.4, 107.55) * mm});
            skLineSegment(sketch, "E87", {"start": v(-4.25, 80) * mm, "end": v(-3.6, 110) * mm});
            skCircle(sketch, "E88", {"center": v(-3.6, 110) * mm, "radius": 6 * mm});
            skPoint(sketch, "E89.start.orphan", {"position": v(-32.8, -107.72) * mm});
            skPoint(sketch, "E90.start.orphan", {"position": v(0, -80) * mm});
            skPoint(sketch, "E91.end.orphan", {"position": v(16.7, -107.72) * mm});
            skPoint(sketch, "E92.end.orphan", {"position": v(60, 0) * mm});
            skPoint(sketch, "E92.start.orphan", {"position": v(-80, 0) * mm});
            skLineSegment(sketch, "E93", {"start": v(-80, 0) * mm, "end": v(80, 0) * mm, "construction": true});
            skLineSegment(sketch, "E94.MirrorCS", {"start": v(-18.4, -98) * mm, "end": v(-18.4, -107.55) * mm});
            skArc(sketch, "E95.MirrorCS", {"start": v(10.43, -115.3) * mm, "mid": v(-7.5, -124.49) * mm, "end": v(-18.4, -107.55) * mm});
            skLineSegment(sketch, "E96.MirrorCS", {"start": v(10.43, -97.57) * mm, "end": v(10.43, -115.3) * mm});
            skLineSegment(sketch, "E97.MirrorCS", {"start": v(28, -80) * mm, "end": v(10.43, -97.57) * mm});
            skLineSegment(sketch, "E98.MirrorCS", {"start": v(-36.4, -80) * mm, "end": v(-18.4, -98) * mm});
            skCircle(sketch, "E99.MirrorC", {"center": v(-3.6, -110) * mm, "radius": 6 * mm});
            skLineSegment(sketch, "E100.MirrorCS", {"start": v(-4.25, -80) * mm, "end": v(-3.6, -110) * mm});
            skSolve(sketch);
        }
        {
            var Q0;
            {var subQ0=sQuery(id+"F16.wireOp",EDGE,"E80");Q0=makeQuery(id+"F16.imprint","IMPRINT",FACE,{"disambiguationData":[TD([[makeQuery(id+"F16.imprint","IMPRINT",EDGE,{"derivedFrom":subQ0}),1.0]])]});}
            var Q1;
            Q1=makeQuery(id+"F16.imprint","IMPRINT",FACE,{"disambiguationData":[TD([[makeQuery(id+"F16.imprint","IMPRINT",EDGE,{"derivedFrom":sQuery(id+"F16.wireOp",EDGE,"E94.MirrorCS")}),1.0]])]});
            var Q2;
            {var subQ10=sQuery(id+"F16.wireOp",EDGE,"E79.1");Q2=makeQuery(id+"F16.imprint","IMPRINT",FACE,{"disambiguationData":[TD([[makeQuery(id+"F16.imprint","IMPRINT",EDGE,{"derivedFrom":subQ10}),1.0]])]});}
            var Q3;
            Q3=makeQuery(id+"F2.opExtrude","CAP_FACE",FACE,{"disambiguationData":[OSD([sQuery(id+"F0.wireOp",EDGE,"E12"),sQuery(id+"F0.wireOp",EDGE,"E13"),sQuery(id+"F0.wireOp",EDGE,"E14"),sQuery(id+"F0.wireOp",EDGE,"E15"),sQuery(id+"F0.wireOp",EDGE,"E17.filletArc"),sQuery(id+"F0.wireOp",EDGE,"E18.filletArc"),sQuery(id+"F0.wireOp",EDGE,"E19.filletArc"),sQuery(id+"F0.wireOp",EDGE,"E20.filletArc"),sQuery(id+"F0.wireOp",EDGE,"E25.0"),sQuery(id+"F0.wireOp",EDGE,"E25.1"),sQuery(id+"F0.wireOp",EDGE,"E25.2"),sQuery(id+"F0.wireOp",EDGE,"E25.3"),sQuery(id+"F0.wireOp",EDGE,"E25.4"),sQuery(id+"F0.wireOp",EDGE,"E25.5"),sQuery(id+"F0.wireOp",EDGE,"E25.6"),sQuery(id+"F0.wireOp",EDGE,"E25.7")])],"isStart":false});
            extrude(context, id + "F17", {"entities" : qUnion([Q0, Q1, Q2]), "endBound" : BoundingType.UP_TO_SURFACE, "endBoundEntityFace" : qUnion([Q3]), "depth" : 25 * mm});
        }
    });
